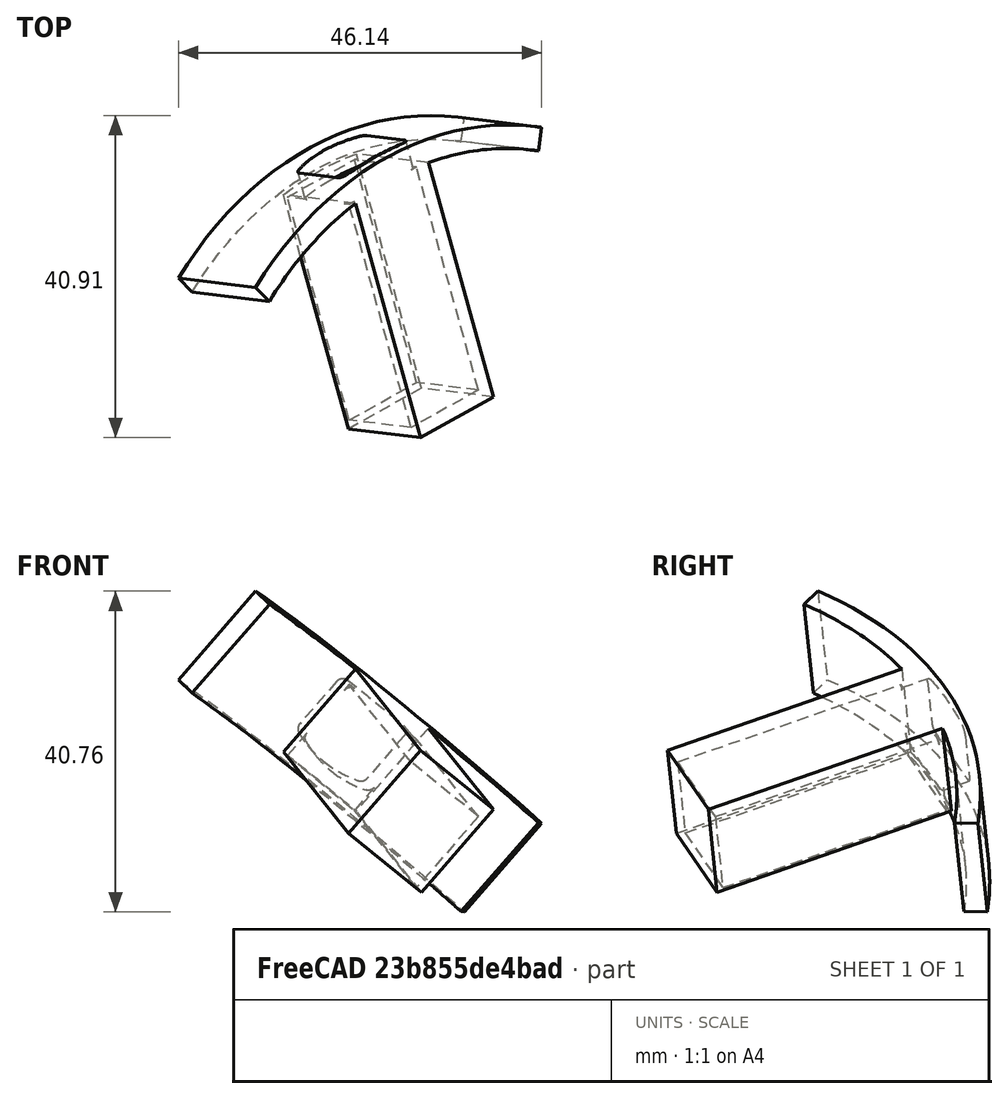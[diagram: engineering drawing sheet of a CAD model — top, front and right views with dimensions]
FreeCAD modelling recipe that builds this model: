
FCSTD DOCUMENT  (FreeCAD 0.16R4924 (Git))
Label: interior_servo_bay_v3p3
License: All rights reserved
LicenseURL: http://en.wikipedia.org/wiki/All_rights_reserved
objects: Part::Cut×3, Part::Cylinder×2, Part::Feature×2, Part::Extrusion×2, Part::MultiFuse×2, Part::Box×2, Part::Thickness×1
note: 14 computed .brp shape members not serialized (recipe doc carries the construction recipe); baked Part::Feature solids carry a one-line shape summary decoded from their .brp

FEATURE [Part::Cylinder] Cylinder  label="bottle_wall"
  Angle = 60
  Height = 15
  Placement = pos=(8.5,-7,0) rot=(0,0,1;1.0472rad)
  Radius = 51
FEATURE [Part::Cylinder] Cylinder001  label="bottle_wall001"
  Angle = 60
  Height = 15
  Placement = pos=(8.5,-7,0) rot=(0,0,1;1.0472rad)
  Radius = 48
FEATURE [Part::Cut] Cut  label="bottle_wall_composite"
  Base = -> Cylinder
  Placement = pos=(0,-2,0) rot=(0,0,1;0rad)
  Tool = -> Cylinder001
FEATURE [Part::Feature] Common_cs  label="pin_cs"
  Placement = pos=(3.5,35,2) rot=(0,0,1;0rad)
  shape: bbox 10 x 2e-07 x 8 mm, 0 faces, 0 solids (baked)
FEATURE [Part::Extrusion] Extrude
  Base = -> Common_cs
  Dir = (0,5,0)
  Solid = true
FEATURE [Part::Thickness] Thickness
  Faces = -> Extrude [Face7]
  Intersection = false
  Join = 0
  Mode = 0
  SelfIntersection = false
  Value = 1
FEATURE [Part::Feature] Common_cs001  label="pin_cs001"
  Placement = pos=(3.5,35,2) rot=(0,0,1;0rad)
  shape: bbox 10 x 2e-07 x 8 mm, 0 faces, 0 solids (baked)
FEATURE [Part::Extrusion] Extrude001
  Base = -> Common_cs001
  Dir = (0,5,0)
  Solid = true
FEATURE [Part::MultiFuse] Fusion  label="bolt_bottle_side_opening"
  Placement = pos=(0,-7,1) rot=(0,0,1;0rad)
  Shapes = -> [Thickness,Extrude,Extrude001]
FEATURE [Part::Box] Box  label="pullBay"
  Height = 15
  Length = 12
  Placement = pos=(2.5,7,2) rot=(0,0,1;0rad)
  Width = 31
FEATURE [Part::Box] Box001  label="Case"
  Height = 14
  Length = 13
  Placement = pos=(2,6,0) rot=(0,0,1;0rad)
  Width = 34
FEATURE [Part::Cut] Cut001  label="cut bay from case"
  Base = -> Box001
  Tool = -> Box
FEATURE [Part::MultiFuse] Fusion001  label="wall plus case"
  Shapes = -> [Cut,Cut001]
FEATURE [Part::Cut] Cut002  label="hole cut out of case"
  Base = -> Fusion001
  Placement = pos=(0,0,0) rot=(-0.188305,0.975433,0.114334;3.82553rad)
  Tool = -> Fusion
